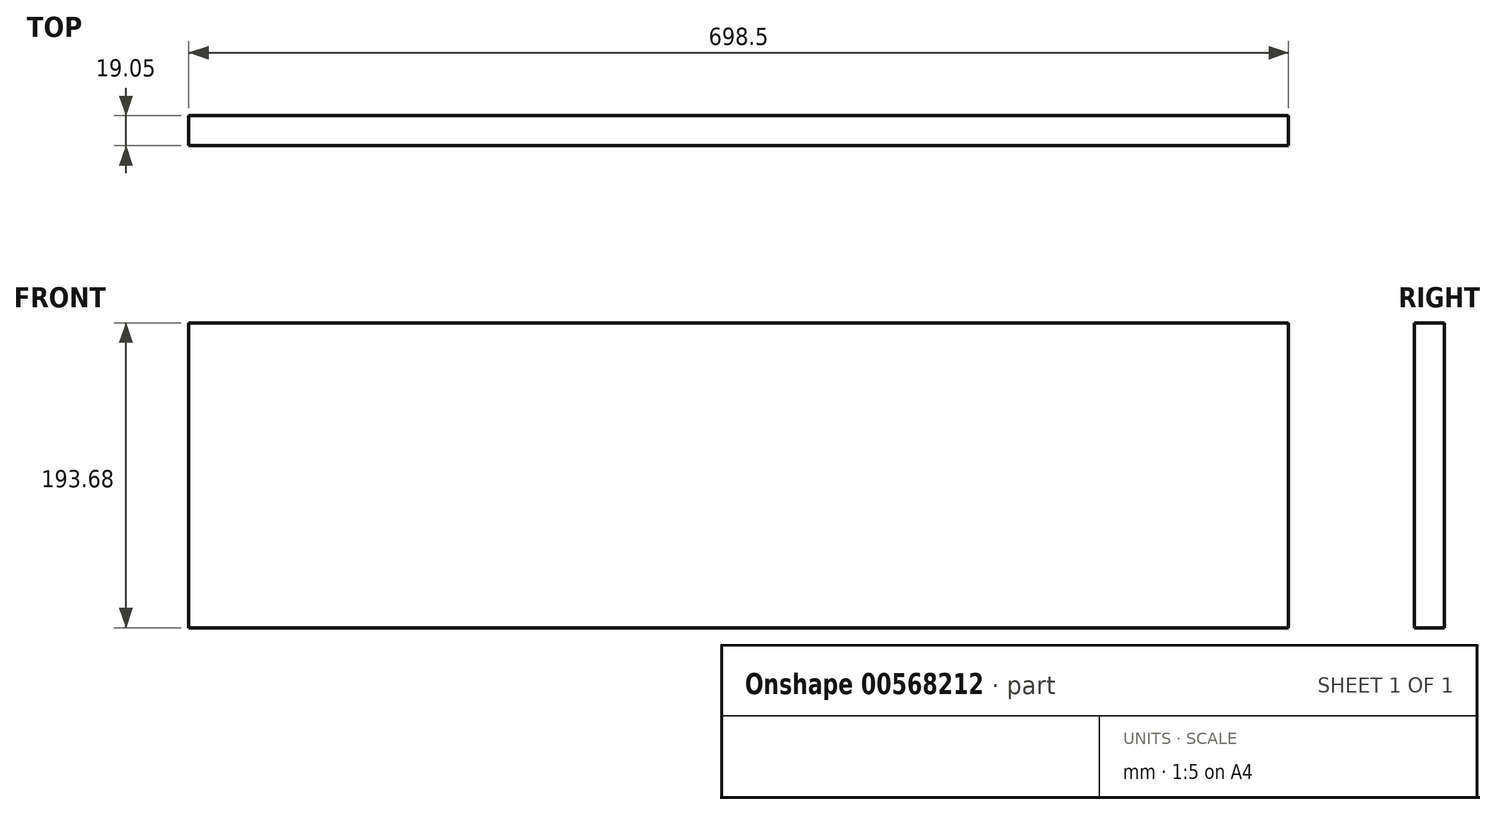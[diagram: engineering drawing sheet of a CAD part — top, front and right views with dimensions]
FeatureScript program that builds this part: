
annotation { "Feature Type Name" : "Feature", "Feature Type Description" : "" }
export const myFeature = defineFeature(function(context is Context, id is Id, definition is map)
    precondition{}
    {
        {
            var Q0;
            Q0=qCreatedBy(makeId("Front.planeOp"),FACE);
            var sketch = newSketch(context, id + "F0", { "sketchPlane" : qUnion([Q0])});
            skLineSegment(sketch, "E0.bottom", {"start": v(0, 0) * mm, "end": v(698.5, 0) * mm});
            skLineSegment(sketch, "E0.top", {"start": v(0, 193.68) * mm, "end": v(698.5, 193.68) * mm});
            skLineSegment(sketch, "E0.left", {"start": v(0, 0) * mm, "end": v(0, 193.68) * mm});
            skLineSegment(sketch, "E0.right", {"start": v(698.5, 0) * mm, "end": v(698.5, 193.68) * mm});
            skSolve(sketch);
        }
        {
            var Q0;
            Q0 = qSketchRegion(id + "F0", true);
            extrude(context, id + "F1", {"entities" : qUnion([Q0]), "depth" : 19.05 * mm, "offsetDistance" : 25.4 * mm});
        }
    });
